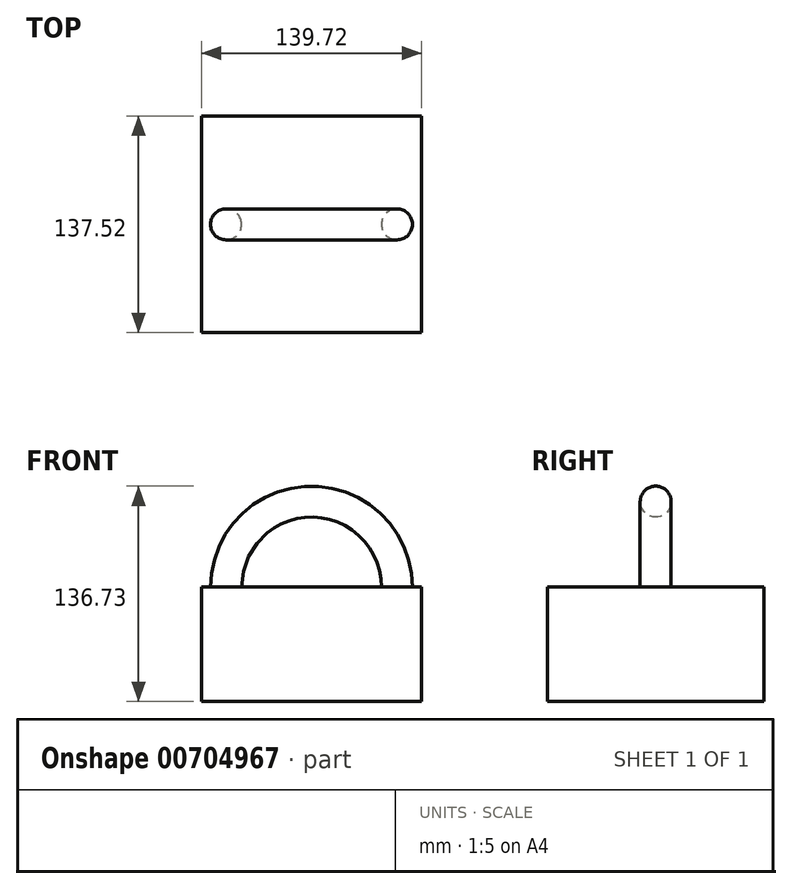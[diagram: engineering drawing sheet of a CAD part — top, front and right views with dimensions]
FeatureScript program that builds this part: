
annotation { "Feature Type Name" : "Feature", "Feature Type Description" : "" }
export const myFeature = defineFeature(function(context is Context, id is Id, definition is map)
    precondition{}
    {
        {
            var Q0;
            Q0=qCreatedBy(makeId("Top.planeOp"),FACE);
            var sketch = newSketch(context, id + "F0", { "sketchPlane" : qUnion([Q0])});
            skLineSegment(sketch, "E0.bottom", {"start": v(69.86, -68.76) * mm, "end": v(-69.86, -68.76) * mm});
            skLineSegment(sketch, "E0.top", {"start": v(69.86, 68.76) * mm, "end": v(-69.86, 68.76) * mm});
            skLineSegment(sketch, "E0.left", {"start": v(69.86, -68.76) * mm, "end": v(69.86, 68.76) * mm});
            skLineSegment(sketch, "E0.right", {"start": v(-69.86, -68.76) * mm, "end": v(-69.86, 68.76) * mm});
            skPoint(sketch, "E0.middle", {"position": v(0, 0) * mm});
            skLineSegment(sketch, "E1", {"start": v(0, 68.76) * mm, "end": v(0, -68.76) * mm});
            skSolve(sketch);
        }
        {
            var Q0;
            Q0=qCreatedBy(makeId("Top.planeOp"),FACE);
            var sketch = newSketch(context, id + "F1", { "sketchPlane" : qUnion([Q0])});
            skCircle(sketch, "E2", {"center": v(54.26, 0) * mm, "radius": 9.82 * mm});
            skSolve(sketch);
        }
        {
            var Q0;
            {var subQ0=sQuery(id+"F0.wireOp",EDGE,"E0.right");Q0=makeQuery(id+"F0.imprint","IMPRINT",FACE,{"disambiguationData":[TD([[makeQuery(id+"F0.imprint","IMPRINT",EDGE,{"derivedFrom":subQ0}),-1.0]])]});}
            var Q1;
            {var subQ0=sQuery(id+"F0.wireOp",EDGE,"E0.left");Q1=makeQuery(id+"F0.imprint","IMPRINT",FACE,{"disambiguationData":[TD([[makeQuery(id+"F0.imprint","IMPRINT",EDGE,{"derivedFrom":subQ0}),1.0]])]});}
            extrude(context, id + "F2", {"entities" : qUnion([Q0, Q1]), "oppositeDirection" : true, "depth" : 72.64 * mm, "offsetDistance" : 25.4 * mm});
        }
        {
            var Q0;
            Q0 = qSketchRegion(id + "F1", true);
            var Q1;
            Q1=sQuery(id+"F0.wireOp",EDGE,"E1");
            revolve(context, id + "F3", {"operationType" : NewBodyOperationType.ADD, "entities" : qUnion([Q0]), "axis" : qUnion([Q1]), "revolveType" : RevolveType.FULL});
        }
    });
